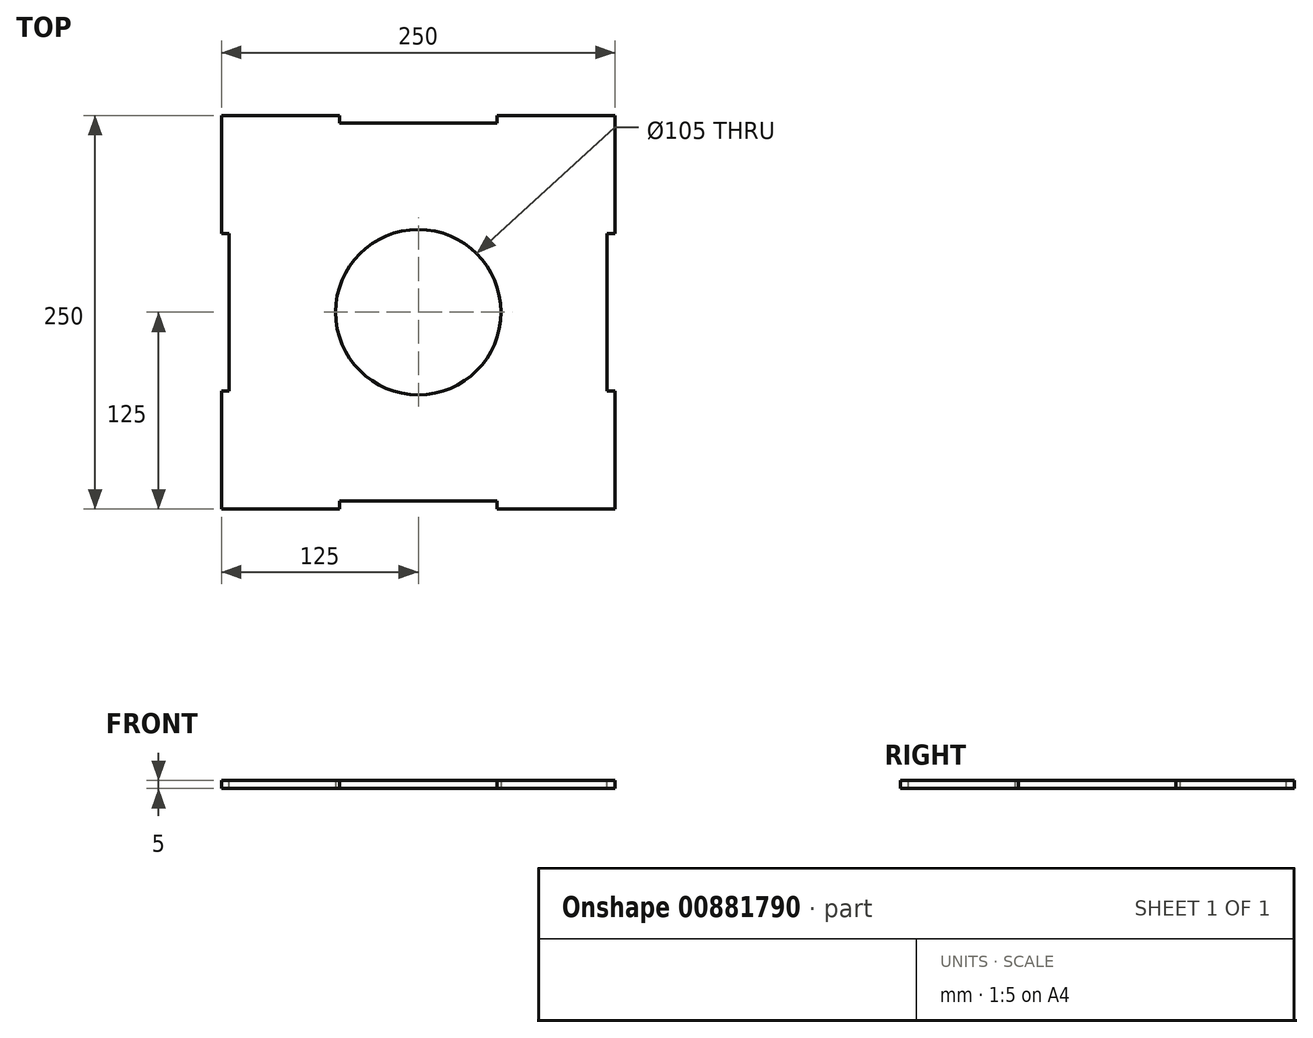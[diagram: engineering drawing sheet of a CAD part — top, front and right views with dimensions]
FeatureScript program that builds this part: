
annotation { "Feature Type Name" : "Feature", "Feature Type Description" : "" }
export const myFeature = defineFeature(function(context is Context, id is Id, definition is map)
    precondition{}
    {
        {
            var Q0;
            Q0=qCreatedBy(makeId("Top.planeOp"),FACE);
            var sketch = newSketch(context, id + "F0", { "sketchPlane" : qUnion([Q0])});
            skLineSegment(sketch, "E0.bottom", {"start": v(125, -125) * mm, "end": v(-125, -125) * mm});
            skLineSegment(sketch, "E0.top", {"start": v(125, 125) * mm, "end": v(-125, 125) * mm});
            skLineSegment(sketch, "E0.left", {"start": v(125, -125) * mm, "end": v(125, 125) * mm});
            skLineSegment(sketch, "E0.right", {"start": v(-125, -125) * mm, "end": v(-125, 125) * mm});
            skPoint(sketch, "E0.middle", {"position": v(0, 0) * mm});
            skCircle(sketch, "E1", {"center": v(0, 0) * mm, "radius": 52.5 * mm});
            skSolve(sketch);
        }
        {
            var Q0;
            Q0=qSketchRegion(id+"F0",true);
            extrude(context, id + "F1", {"entities" : qUnion([Q0]), "depth" : 5 * mm, "offsetDistance" : 25 * mm});
        }
        {
            var Q0;
            Q0=makeQuery(id+"F1.opExtrude","CAP_FACE",FACE,{"disambiguationData":[OSD([sQuery(id+"F0.wireOp",EDGE,"E0.bottom"),sQuery(id+"F0.wireOp",EDGE,"E0.top"),sQuery(id+"F0.wireOp",EDGE,"E0.left"),sQuery(id+"F0.wireOp",EDGE,"E0.right"),sQuery(id+"F0.wireOp",EDGE,"E1")])],"isStart":false});
            var sketch = newSketch(context, id + "F2", { "sketchPlane" : qUnion([Q0])});
            skLineSegment(sketch, "E2", {"start": v(-125, 0) * mm, "end": v(-99.92, 0) * mm, "construction": true});
            skLineSegment(sketch, "E3", {"start": v(0, 125) * mm, "end": v(0, 71.6) * mm, "construction": true});
            skLineSegment(sketch, "E4", {"start": v(-50, 125) * mm, "end": v(-50, 120) * mm});
            skLineSegment(sketch, "E5", {"start": v(-50, 120) * mm, "end": v(0, 120) * mm});
            skLineSegment(sketch, "E6.MirrorCS", {"start": v(50, 120) * mm, "end": v(0, 120) * mm});
            skLineSegment(sketch, "E7.MirrorCS", {"start": v(50, 125) * mm, "end": v(50, 120) * mm});
            skLineSegment(sketch, "E8", {"start": v(-50, 125) * mm, "end": v(0, 125) * mm});
            skLineSegment(sketch, "E9.MirrorCS", {"start": v(50, 125) * mm, "end": v(0, 125) * mm});
            skLineSegment(sketch, "E10", {"start": v(-125, 50) * mm, "end": v(-120, 50) * mm});
            skLineSegment(sketch, "E11", {"start": v(-120, 50) * mm, "end": v(-120, 0) * mm});
            skLineSegment(sketch, "E12", {"start": v(-125, 50) * mm, "end": v(-125, 0) * mm});
            skLineSegment(sketch, "E13.MirrorCS", {"start": v(-120, -50) * mm, "end": v(-120, 0) * mm});
            skLineSegment(sketch, "E14.MirrorCS", {"start": v(-125, -50) * mm, "end": v(-125, 0) * mm});
            skLineSegment(sketch, "E15.MirrorCS", {"start": v(-125, -50) * mm, "end": v(-120, -50) * mm});
            skLineSegment(sketch, "E16.MirrorCS", {"start": v(-50, -125) * mm, "end": v(-50, -120) * mm});
            skLineSegment(sketch, "E17.MirrorCS", {"start": v(-50, -120) * mm, "end": v(0, -120) * mm});
            skLineSegment(sketch, "E18.MirrorCS", {"start": v(-50, -125) * mm, "end": v(0, -125) * mm});
            skLineSegment(sketch, "E19.MirrorCS", {"start": v(50, -125) * mm, "end": v(0, -125) * mm});
            skLineSegment(sketch, "E20.MirrorCS", {"start": v(50, -120) * mm, "end": v(0, -120) * mm});
            skLineSegment(sketch, "E21.MirrorCS", {"start": v(50, -125) * mm, "end": v(50, -120) * mm});
            skLineSegment(sketch, "E22.MirrorCS", {"start": v(125, -50) * mm, "end": v(125, 0) * mm});
            skLineSegment(sketch, "E23.MirrorCS", {"start": v(125, -50) * mm, "end": v(120, -50) * mm});
            skLineSegment(sketch, "E24.MirrorCS", {"start": v(120, -50) * mm, "end": v(120, 0) * mm});
            skLineSegment(sketch, "E25.MirrorCS", {"start": v(125, 50) * mm, "end": v(125, 0) * mm});
            skLineSegment(sketch, "E26.MirrorCS", {"start": v(125, 50) * mm, "end": v(120, 50) * mm});
            skLineSegment(sketch, "E27.MirrorCS", {"start": v(120, 50) * mm, "end": v(120, 0) * mm});
            skSolve(sketch);
        }
        {
            var Q0;
            Q0=qSketchRegion(id+"F2",true);
            extrude(context, id + "F3", {"entities" : qUnion([Q0]), "operationType" : NewBodyOperationType.REMOVE, "endBound" : BoundingType.THROUGH_ALL, "oppositeDirection" : true, "depth" : 25 * mm, "offsetDistance" : 25 * mm});
        }
    });
